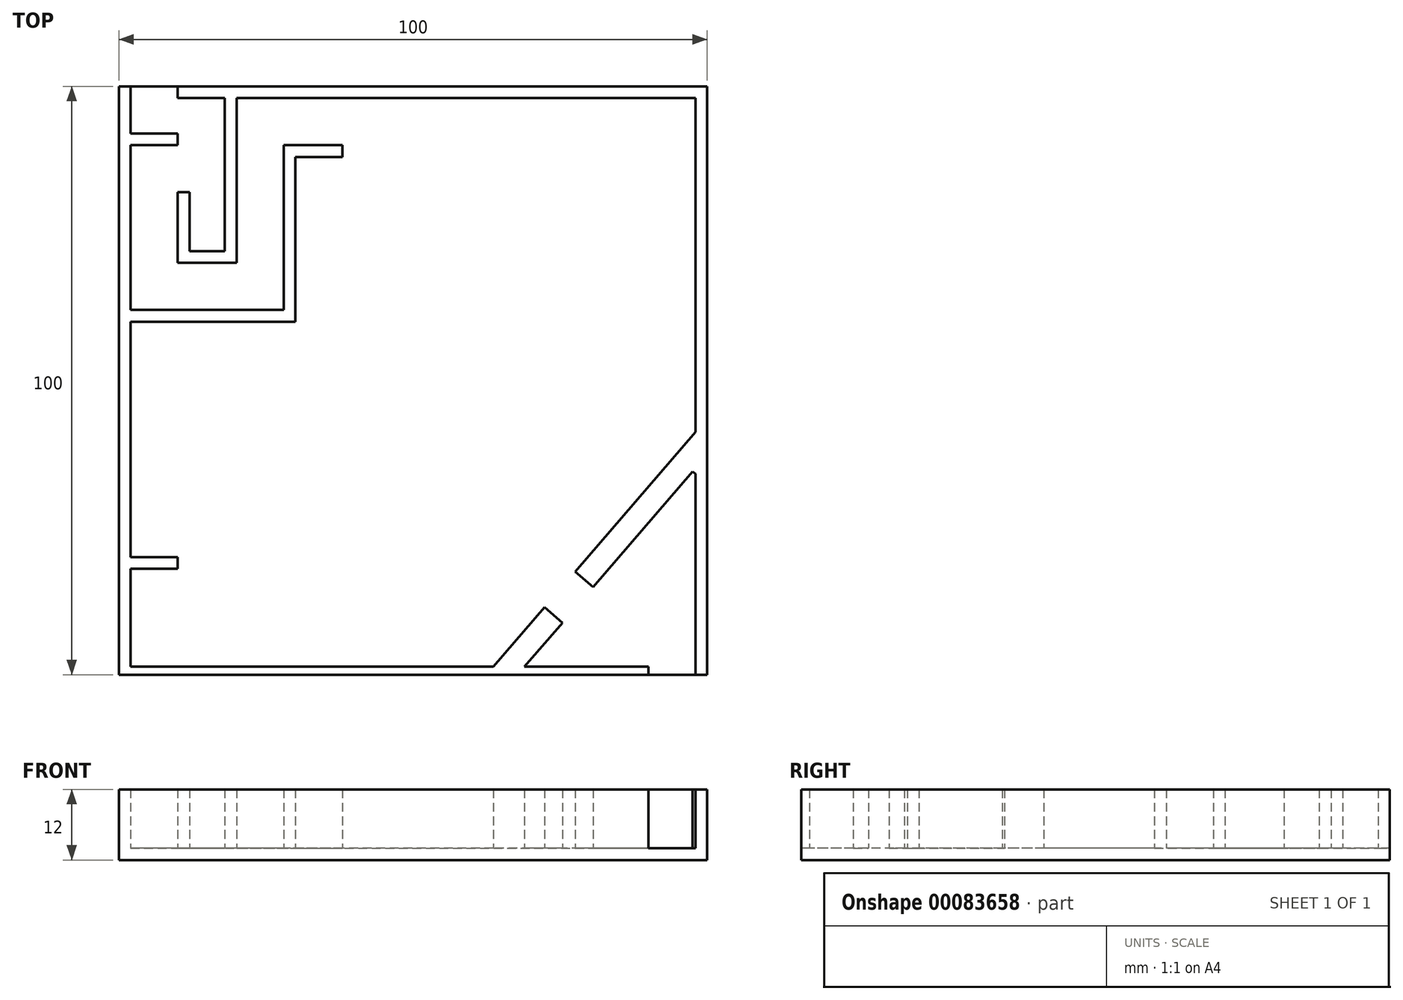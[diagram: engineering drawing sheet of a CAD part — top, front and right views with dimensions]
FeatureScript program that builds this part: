
annotation { "Feature Type Name" : "Feature", "Feature Type Description" : "" }
export const myFeature = defineFeature(function(context is Context, id is Id, definition is map)
    precondition{}
    {
        {
            var Q0;
            Q0=qCreatedBy(makeId("Top.planeOp"),FACE);
            var sketch = newSketch(context, id + "F0", { "sketchPlane" : qUnion([Q0])});
            skLineSegment(sketch, "E0.bottom", {"start": v(-50, 50) * mm, "end": v(50, 50) * mm});
            skLineSegment(sketch, "E0.top", {"start": v(-50, -50) * mm, "end": v(50, -50) * mm});
            skLineSegment(sketch, "E0.left", {"start": v(-50, 50) * mm, "end": v(-50, -50) * mm});
            skLineSegment(sketch, "E0.right", {"start": v(50, 50) * mm, "end": v(50, -50) * mm});
            skPoint(sketch, "E0.middle", {"position": v(0, 0) * mm});
            skSolve(sketch);
        }
        {
            var Q0;
            Q0 = qSketchRegion(id + "F0", true);
            extrude(context, id + "F1", {"entities" : qUnion([Q0]), "depth" : 2 * mm});
        }
        {
            var Q0;
            Q0=makeQuery(id+"F1.opExtrude","CAP_FACE",FACE,{"disambiguationData":[OSD([sQuery(id+"F0.wireOp",EDGE,"E0.bottom"),sQuery(id+"F0.wireOp",EDGE,"E0.top"),sQuery(id+"F0.wireOp",EDGE,"E0.left"),sQuery(id+"F0.wireOp",EDGE,"E0.right")])],"isStart":false});
            var sketch = newSketch(context, id + "F2", { "sketchPlane" : qUnion([Q0])});
            skLineSegment(sketch, "E1", {"start": v(-50, 50) * mm, "end": v(-48, 50) * mm});
            skLineSegment(sketch, "E2", {"start": v(-48, 50) * mm, "end": v(-48, -50) * mm});
            skLineSegment(sketch, "E3", {"start": v(-48, -50) * mm, "end": v(-50, -50) * mm});
            skLineSegment(sketch, "E4", {"start": v(-50, -50) * mm, "end": v(-50, 50) * mm});
            skLineSegment(sketch, "E5", {"start": v(48, -50) * mm, "end": v(50, -50) * mm});
            skLineSegment(sketch, "E6", {"start": v(50, 50) * mm, "end": v(-40, 50) * mm});
            skLineSegment(sketch, "E7", {"start": v(-40, 48) * mm, "end": v(-40, 50) * mm});
            skLineSegment(sketch, "E8", {"start": v(40, -48.66) * mm, "end": v(40, -50) * mm});
            skLineSegment(sketch, "E9", {"start": v(-48, 50) * mm, "end": v(-48, 42) * mm});
            skLineSegment(sketch, "E10", {"start": v(-48, 42) * mm, "end": v(-40, 42) * mm});
            skLineSegment(sketch, "E11", {"start": v(-40, 42) * mm, "end": v(-40, 40) * mm});
            skLineSegment(sketch, "E12", {"start": v(-40, 40) * mm, "end": v(-48, 40) * mm});
            skLineSegment(sketch, "E13", {"start": v(-50, -50) * mm, "end": v(-50, -32) * mm});
            skLineSegment(sketch, "E14", {"start": v(-50, -32) * mm, "end": v(-40, -32) * mm});
            skLineSegment(sketch, "E15", {"start": v(-40, -32) * mm, "end": v(-40, -30) * mm});
            skLineSegment(sketch, "E16", {"start": v(-40, -30) * mm, "end": v(-50, -30) * mm});
            skLineSegment(sketch, "E17", {"start": v(-40, 50) * mm, "end": v(-30, 50) * mm});
            skLineSegment(sketch, "E18", {"start": v(-30, 50) * mm, "end": v(-30, 20) * mm});
            skLineSegment(sketch, "E19", {"start": v(-30, 20) * mm, "end": v(-40, 20) * mm});
            skLineSegment(sketch, "E20", {"start": v(-40, 20) * mm, "end": v(-40, 22) * mm});
            skLineSegment(sketch, "E21", {"start": v(-40, 22) * mm, "end": v(-32, 22) * mm});
            skLineSegment(sketch, "E22", {"start": v(-32, 22) * mm, "end": v(-32, 50) * mm});
            skLineSegment(sketch, "E23", {"start": v(-40, 22) * mm, "end": v(-40, 32) * mm});
            skLineSegment(sketch, "E24", {"start": v(-40, 32) * mm, "end": v(-38, 32) * mm});
            skLineSegment(sketch, "E25", {"start": v(-38, 32) * mm, "end": v(-38, 22) * mm});
            skLineSegment(sketch, "E26", {"start": v(-48, 40) * mm, "end": v(-48, 10) * mm});
            skLineSegment(sketch, "E27", {"start": v(-48, 10) * mm, "end": v(-20, 10) * mm});
            skLineSegment(sketch, "E28", {"start": v(-20, 10) * mm, "end": v(-20, 38) * mm});
            skLineSegment(sketch, "E29", {"start": v(-20, 38) * mm, "end": v(-12, 38) * mm});
            skLineSegment(sketch, "E30", {"start": v(-12, 38) * mm, "end": v(-12, 40) * mm});
            skLineSegment(sketch, "E31", {"start": v(-12, 40) * mm, "end": v(-22, 40) * mm});
            skLineSegment(sketch, "E32", {"start": v(-22, 40) * mm, "end": v(-22, 12) * mm});
            skLineSegment(sketch, "E33", {"start": v(-22, 12) * mm, "end": v(-48, 12) * mm});
            skLineSegment(sketch, "E34", {"start": v(-40, 48) * mm, "end": v(-32, 48) * mm});
            skLineSegment(sketch, "E35", {"start": v(-30, 50) * mm, "end": v(-30, 48) * mm});
            skLineSegment(sketch, "E36", {"start": v(-30, 48) * mm, "end": v(48, 48) * mm});
            skLineSegment(sketch, "E37", {"start": v(48, 48) * mm, "end": v(48, -50) * mm});
            skLineSegment(sketch, "E38", {"start": v(50, -50) * mm, "end": v(50, 50) * mm});
            skLineSegment(sketch, "E39", {"start": v(40, -48.66) * mm, "end": v(-48, -48.66) * mm});
            skLineSegment(sketch, "E40", {"start": v(40, -50) * mm, "end": v(-48, -50) * mm});
            skLineSegment(sketch, "E41", {"start": v(48, -8.78) * mm, "end": v(27.56, -32.5) * mm});
            skLineSegment(sketch, "E42", {"start": v(27.56, -32.5) * mm, "end": v(30.59, -35.12) * mm});
            skLineSegment(sketch, "E43", {"start": v(30.59, -35.12) * mm, "end": v(47.52, -15.47) * mm});
            skLineSegment(sketch, "E44", {"start": v(47.52, -15.47) * mm, "end": v(48, -15.88) * mm});
            skLineSegment(sketch, "E45", {"start": v(48, -15.88) * mm, "end": v(48, -8.78) * mm});
            skLineSegment(sketch, "E46", {"start": v(25.37, -41.18) * mm, "end": v(22.34, -38.57) * mm});
            skLineSegment(sketch, "E47", {"start": v(22.34, -38.57) * mm, "end": v(13.64, -48.66) * mm});
            skLineSegment(sketch, "E48", {"start": v(25.37, -41.18) * mm, "end": v(18.92, -48.66) * mm});
            skSolve(sketch);
        }
        {
            var Q0;
            Q0 = qSketchRegion(id + "F2", true);
            extrude(context, id + "F3", {"entities" : qUnion([Q0]), "operationType" : NewBodyOperationType.ADD, "depth" : 10 * mm});
        }
    });
